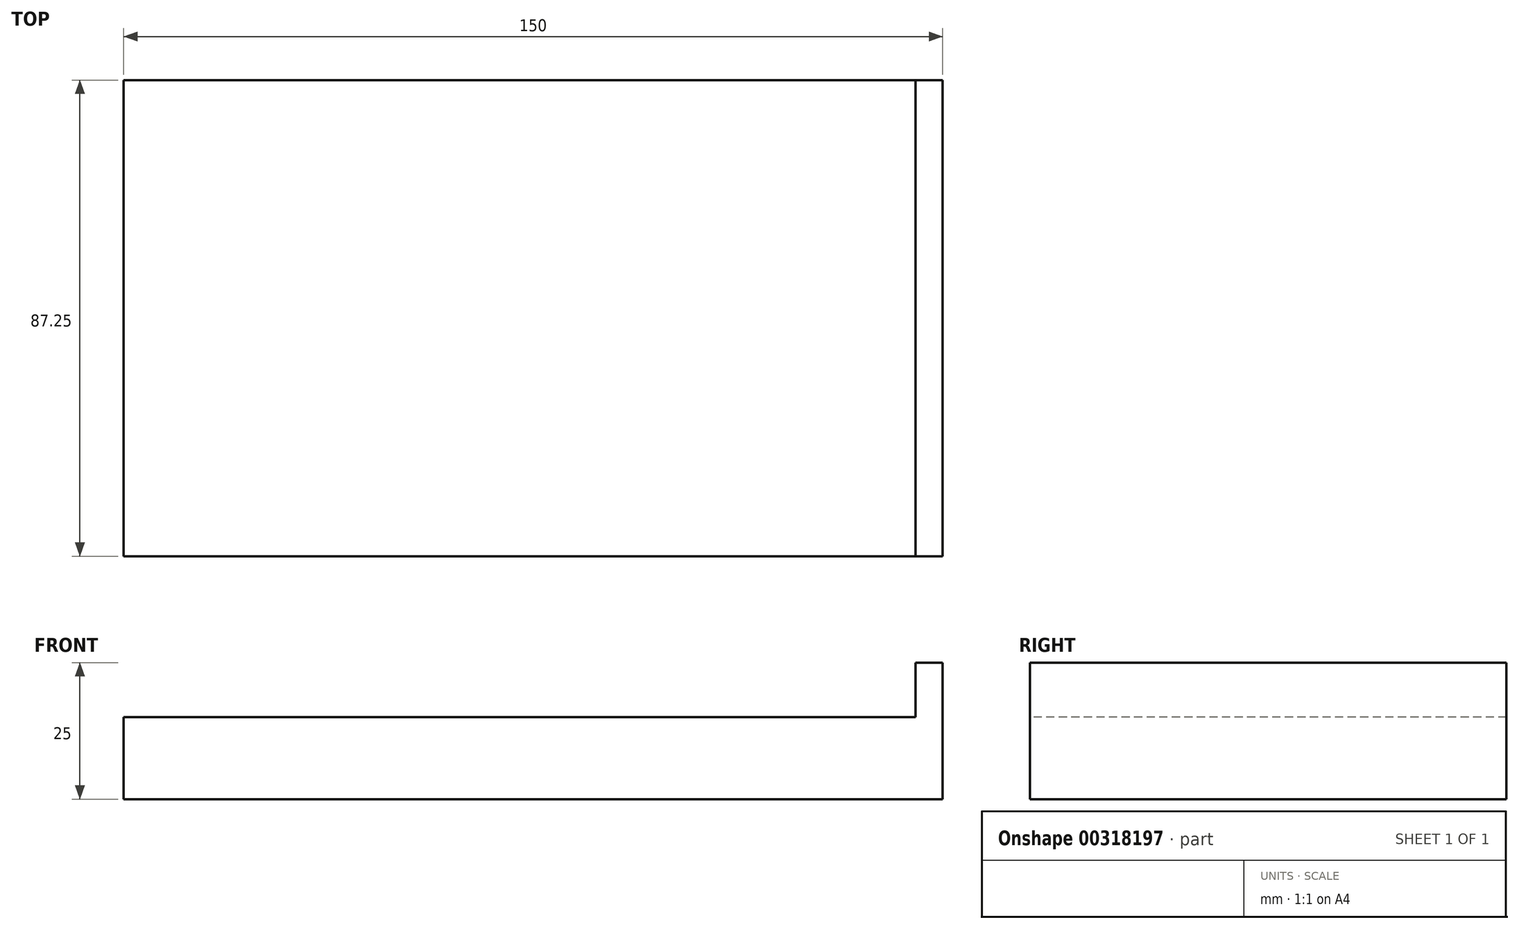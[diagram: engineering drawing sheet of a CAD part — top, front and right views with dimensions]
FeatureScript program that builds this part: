
annotation { "Feature Type Name" : "Feature", "Feature Type Description" : "" }
export const myFeature = defineFeature(function(context is Context, id is Id, definition is map)
    precondition{}
    {
        {
            var Q0;
            Q0=qCreatedBy(makeId("Front.planeOp"),FACE);
            var sketch = newSketch(context, id + "F0", { "sketchPlane" : qUnion([Q0])});
            skLineSegment(sketch, "E0.bottom", {"start": v(75, -7.5) * mm, "end": v(-75, -7.5) * mm});
            skLineSegment(sketch, "E0.top", {"start": v(75, 7.5) * mm, "end": v(-75, 7.5) * mm});
            skLineSegment(sketch, "E0.left", {"start": v(75, -7.5) * mm, "end": v(75, 7.5) * mm});
            skLineSegment(sketch, "E0.right", {"start": v(-75, -7.5) * mm, "end": v(-75, 7.5) * mm});
            skPoint(sketch, "E0.middle", {"position": v(0, 0) * mm});
            skSolve(sketch);
        }
        {
            var Q0;
            Q0=makeQuery(id+"F0.imprint","IMPRINT",FACE,{"disambiguationData":[TD([[makeQuery(id+"F0.imprint","IMPRINT",EDGE,{"derivedFrom":sQuery(id+"F0.wireOp",EDGE,"E0.bottom")}),-1.0]])]});
            extrude(context, id + "F1", {"entities" : qUnion([Q0]), "depth" : 87.25 * mm});
        }
        {
            var Q0;
            Q0=makeQuery(id+"F1.opExtrude","SWEPT_FACE",FACE,{"disambiguationData":[OSD([sQuery(id+"F0.wireOp",EDGE,"E0.top")])]});
            var sketch = newSketch(context, id + "F2", { "sketchPlane" : qUnion([Q0])});
            skLineSegment(sketch, "E1.0", {"start": v(75, 0) * mm, "end": v(-75, 0) * mm});
            skLineSegment(sketch, "E2.0", {"start": v(75, -87.25) * mm, "end": v(75, 0) * mm});
            skLineSegment(sketch, "E3.0", {"start": v(75, -87.25) * mm, "end": v(-75, -87.25) * mm});
            skLineSegment(sketch, "E4.0", {"start": v(-75, -87.25) * mm, "end": v(-75, 0) * mm});
            skLineSegment(sketch, "E5", {"start": v(70, 0) * mm, "end": v(70, -87.25) * mm});
            skSolve(sketch);
        }
        {
            var Q0;
            {var subQ0=sQuery(id+"F2.wireOp",EDGE,"E2.0");Q0=makeQuery(id+"F2.imprint","IMPRINT",FACE,{"disambiguationData":[TD([[makeQuery(id+"F2.imprint","IMPRINT",EDGE,{"derivedFrom":subQ0}),1.0]])]});}
            extrude(context, id + "F3", {"entities" : qUnion([Q0]), "operationType" : NewBodyOperationType.ADD, "depth" : 10 * mm, "hasSecondDirection" : true, "secondDirectionOppositeDirection" : true, "secondDirectionDepth" : 10 * mm});
        }
    });
